# Revit family: NLRS_50_ME_UH_buffervat 40 liter - WPSK40_komfort_nathan
name_source: partatom
category: Mechanical Equipment
units: mm (PartAtom-declared; Revit-internal decimal feet)

## family parameters
Always vertical = Yes
Cut with Voids When Loaded = No
OmniClass Number = 23.75.10.34.11
OmniClass Title = Energy Storage Tanks
Part Type = Normal
Room Calculation Point = No
Round Connector Dimension = Use Diameter
Shared = No
Work Plane-Based = No

## types (1)
- WPSK40
    Black = Color RGB 055-055-055
    Central Heating/Cooling Water Inlet = 25 mm  [stored 0.082021 ft]
    Central Heating/Cooling Water Outlet = 25 mm  [stored 0.082021 ft]
    Custom = No
    D1 Description = 1''
    D2 Description = 1''
    Description = Serieel buffervat WPSK 40
    Diameter = 445 mm
    Grey = Color RGB 120-120-120
    Height = 495 mm  [stored 1.62402 ft]
    IFCExportAs = IfcTank
    IFCExportType = NOTDEFINED
    Manufacturer = Komfort
    Max. Tank Operating Pressure (bar) = 6.0 bar
    Model = WPSK 40
    NLRS_C_ETIM_code = EC012339
    NLRS_C_description = CV-buffervat WPSK 40
    NLRS_C_fabrikant_gln_code = 8718347700003
    NLRS_C_fabrikant_product_code = 58005040
    NLRS_C_gtin_code = 08718347709310
    URL = www.nathan.nl
    Unit Weight (kg) = 16.00 kg
    Use Nominal Diameter = Yes
    Volume (L) = 38.5 L
    White = Color RGB 220-220-220

note: [stored X ft] marks values corroborated as IEEE doubles in the binary element streams (Revit-internal decimal feet)

## geometry (parser evidence)
native form markers: Sweep x6
no freeform markers — native parametric forms only
